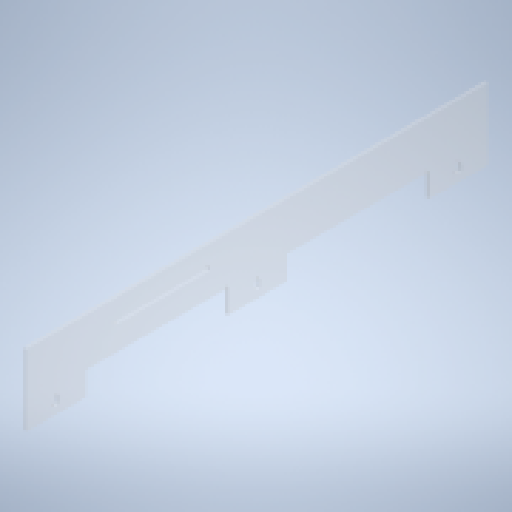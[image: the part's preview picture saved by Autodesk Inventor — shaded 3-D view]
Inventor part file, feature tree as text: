
AUTODESK INVENTOR PART (.ipt)
format: ipt  version: 2024 (Build 280153000, 153)  size: 204,288 bytes
history: native  units: mm
features: extrude x3, sketch x3, other x1
ambient origin geometry x8: Origin, YZ Plane, XZ Plane, XY Plane, X Axis, Y Axis, Z Axis, Center Point
bodies: Body1 (feature_tree)
feature tree (7):
  other  "솔리드1"
  extrude  "돌출1"  Depth=60.0mm
  extrude  "돌출2"  Depth=390.0mm
  extrude  "돌출3"  Depth=30.0mm
  sketch  "스케치1"
  sketch  "스케치2"
  sketch  "스케치3"
